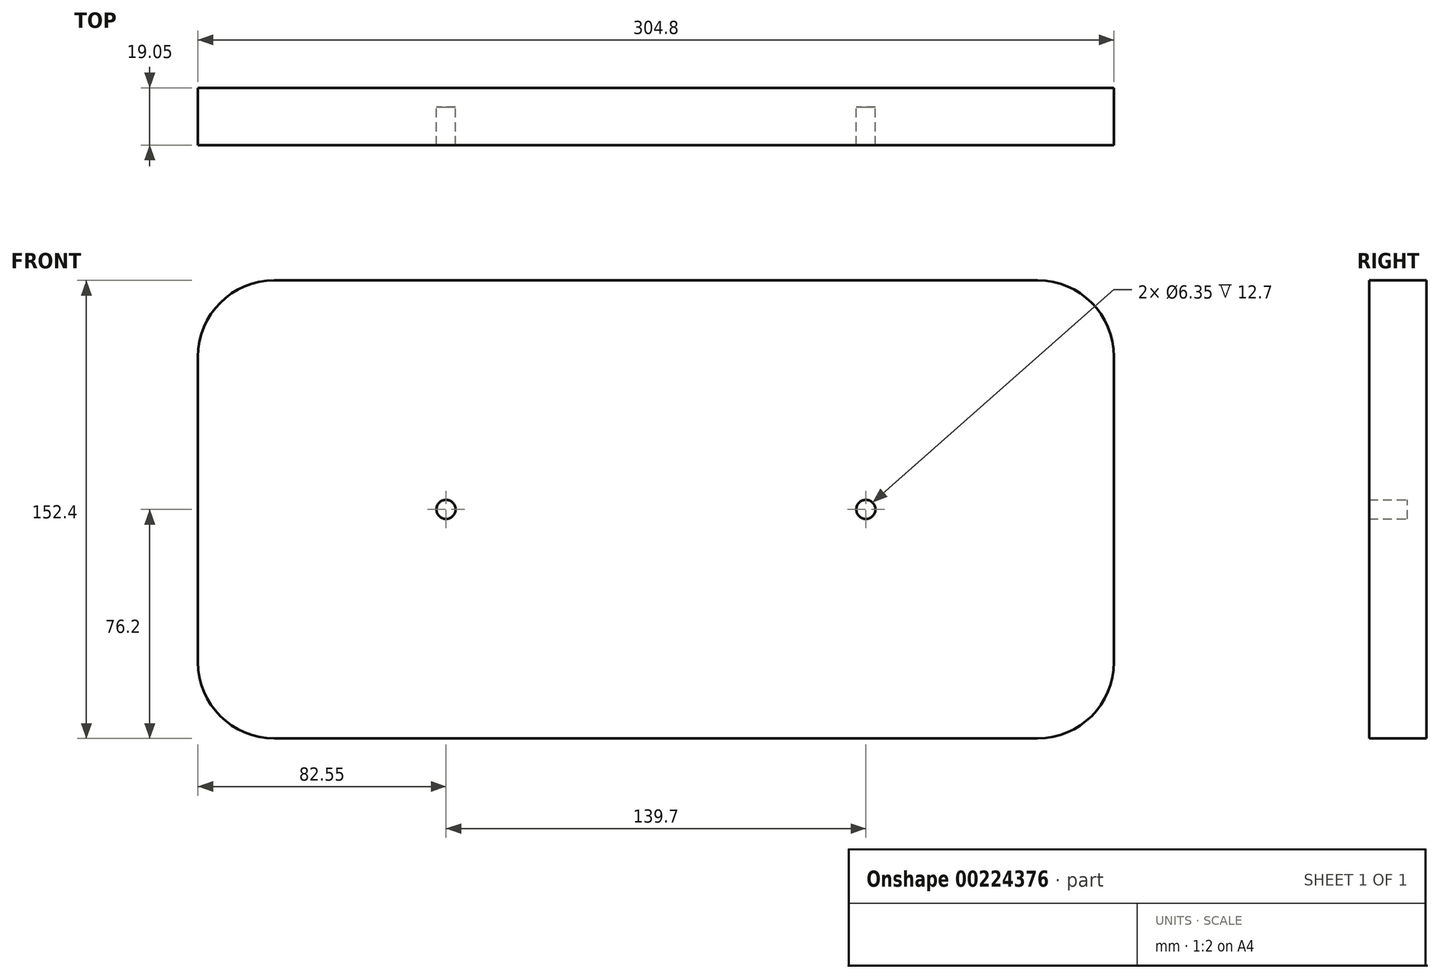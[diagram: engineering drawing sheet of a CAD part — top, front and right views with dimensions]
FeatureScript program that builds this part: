
annotation { "Feature Type Name" : "Feature", "Feature Type Description" : "" }
export const myFeature = defineFeature(function(context is Context, id is Id, definition is map)
    precondition{}
    {
        {
            var Q0;
            Q0=qCreatedBy(makeId("Front.planeOp"),FACE);
            var sketch = newSketch(context, id + "F0", { "sketchPlane" : qUnion([Q0])});
            skLineSegment(sketch, "E0.bottom", {"start": v(25.4, 0) * mm, "end": v(279.4, 0) * mm});
            skLineSegment(sketch, "E0.top", {"start": v(25.4, 152.4) * mm, "end": v(279.4, 152.4) * mm});
            skLineSegment(sketch, "E0.left", {"start": v(0, 25.4) * mm, "end": v(0, 127) * mm});
            skLineSegment(sketch, "E0.right", {"start": v(304.8, 25.4) * mm, "end": v(304.8, 127) * mm});
            skPoint(sketch, "E1.visualSharp", {"position": v(0, 0) * mm});
            skArc(sketch, "E1.filletArc", {"start": v(0, 25.4) * mm, "mid": v(7.44, 7.44) * mm, "end": v(25.4, 0) * mm});
            skPoint(sketch, "E2.visualSharp", {"position": v(0, 152.4) * mm});
            skArc(sketch, "E2.filletArc", {"start": v(25.4, 152.4) * mm, "mid": v(7.44, 144.96) * mm, "end": v(0, 127) * mm});
            skPoint(sketch, "E3.visualSharp", {"position": v(304.8, 152.4) * mm});
            skArc(sketch, "E3.filletArc", {"start": v(304.8, 127) * mm, "mid": v(297.36, 144.96) * mm, "end": v(279.4, 152.4) * mm});
            skPoint(sketch, "E4.visualSharp", {"position": v(304.8, 0) * mm});
            skArc(sketch, "E4.filletArc", {"start": v(279.4, 0) * mm, "mid": v(297.36, 7.44) * mm, "end": v(304.8, 25.4) * mm});
            skLineSegment(sketch, "E5.bottom", {"start": v(31.75, 146.05) * mm, "end": v(273.05, 146.05) * mm});
            skLineSegment(sketch, "E5.top", {"start": v(31.75, 6.35) * mm, "end": v(273.05, 6.35) * mm});
            skLineSegment(sketch, "E5.left", {"start": v(6.35, 120.65) * mm, "end": v(6.35, 31.75) * mm});
            skLineSegment(sketch, "E5.right", {"start": v(298.45, 120.65) * mm, "end": v(298.45, 31.75) * mm});
            skPoint(sketch, "E6.visualSharp", {"position": v(6.35, 146.05) * mm});
            skArc(sketch, "E6.filletArc", {"start": v(31.75, 146.05) * mm, "mid": v(13.79, 138.61) * mm, "end": v(6.35, 120.65) * mm});
            skPoint(sketch, "E7.visualSharp", {"position": v(6.35, 6.35) * mm});
            skArc(sketch, "E7.filletArc", {"start": v(6.35, 31.75) * mm, "mid": v(13.79, 13.79) * mm, "end": v(31.75, 6.35) * mm});
            skPoint(sketch, "E8.visualSharp", {"position": v(298.45, 146.05) * mm});
            skArc(sketch, "E8.filletArc", {"start": v(298.45, 120.65) * mm, "mid": v(291.01, 138.61) * mm, "end": v(273.05, 146.05) * mm});
            skPoint(sketch, "E9.visualSharp", {"position": v(298.45, 6.35) * mm});
            skArc(sketch, "E9.filletArc", {"start": v(273.05, 6.35) * mm, "mid": v(291.01, 13.79) * mm, "end": v(298.45, 31.75) * mm});
            skLineSegment(sketch, "E10", {"start": v(0, 76.2) * mm, "end": v(304.8, 76.2) * mm});
            skSolve(sketch);
        }
        {
            var Q0;
            Q0 = qSketchRegion(id + "F0", true);
            extrude(context, id + "F1", {"entities" : qUnion([Q0]), "depth" : 19.05 * mm});
        }
        {
            var Q0;
            Q0=makeQuery(id+"F0.imprint","IMPRINT",FACE,{"disambiguationData":[TD([[makeQuery(id+"F0.imprint","IMPRINT",EDGE,{"derivedFrom":sQuery(id+"F0.wireOp",EDGE,"E5.bottom")}),-1.0]])]});
            var Q1;
            Q1=makeQuery(id+"F0.imprint","IMPRINT",FACE,{"disambiguationData":[TD([[makeQuery(id+"F0.imprint","IMPRINT",EDGE,{"derivedFrom":sQuery(id+"F0.wireOp",EDGE,"E5.top")}),1.0]])]});
            extrude(context, id + "F2", {"entities" : qUnion([Q0, Q1]), "operationType" : NewBodyOperationType.ADD, "depth" : 6.35 * mm});
        }
        {
            var Q0;
            Q0=makeQuery(id+"F2.opExtrude","CAP_FACE",FACE,{"disambiguationData":[OSD([sQuery(id+"F0.wireOp",EDGE,"E5.bottom"),sQuery(id+"F0.wireOp",EDGE,"E5.top"),sQuery(id+"F0.wireOp",EDGE,"E5.left"),sQuery(id+"F0.wireOp",EDGE,"E5.right"),sQuery(id+"F0.wireOp",EDGE,"E6.filletArc"),sQuery(id+"F0.wireOp",EDGE,"E7.filletArc"),sQuery(id+"F0.wireOp",EDGE,"E8.filletArc"),sQuery(id+"F0.wireOp",EDGE,"E9.filletArc")])],"isStart":false});
            var sketch = newSketch(context, id + "F3", { "sketchPlane" : qUnion([Q0])});
            skLineSegment(sketch, "E11", {"start": v(6.35, 76.2) * mm, "end": v(298.45, 76.2) * mm});
            skCircle(sketch, "E12", {"center": v(82.55, 76.2) * mm, "radius": 3.18 * mm});
            skCircle(sketch, "E13", {"center": v(158.75, 76.2) * mm, "radius": 3.18 * mm});
            skCircle(sketch, "E14", {"center": v(222.25, 76.2) * mm, "radius": 3.18 * mm});
            skSolve(sketch);
        }
        {
            var Q0;
            {var subQ0=sQuery(id+"F3.wireOp",EDGE,"E12");var subQ1=sQuery(id+"F3.wireOp",EDGE,"E11");var subQ2=makeQuery(id+"F3.imprint","INTERSECT",VERTEX,{"disambiguationData":[OD(0.0)],"derivedFrom":[subQ1,subQ0]});Q0=makeQuery(id+"F3.imprint","IMPRINT",FACE,{"disambiguationData":[TD([[makeQuery(id+"F3.imprint","IMPRINT",EDGE,{"disambiguationData":[TD([[subQ2,-1.0]])],"derivedFrom":subQ1}),1.0]])]});}
            var Q1;
            {var subQ0=sQuery(id+"F3.wireOp",EDGE,"E12");var subQ1=sQuery(id+"F3.wireOp",EDGE,"E11");var subQ2=makeQuery(id+"F3.imprint","INTERSECT",VERTEX,{"disambiguationData":[OD(0.0)],"derivedFrom":[subQ1,subQ0]});Q1=makeQuery(id+"F3.imprint","IMPRINT",FACE,{"disambiguationData":[TD([[makeQuery(id+"F3.imprint","IMPRINT",EDGE,{"disambiguationData":[TD([[subQ2,-1.0]])],"derivedFrom":subQ1}),-1.0]])]});}
            var Q2;
            {var subQ0=sQuery(id+"F3.wireOp",EDGE,"E13");var subQ1=sQuery(id+"F3.wireOp",EDGE,"E11");var subQ2=makeQuery(id+"F3.imprint","INTERSECT",VERTEX,{"disambiguationData":[OD(0.0)],"derivedFrom":[subQ1,subQ0]});Q2=makeQuery(id+"F3.imprint","IMPRINT",FACE,{"disambiguationData":[TD([[makeQuery(id+"F3.imprint","IMPRINT",EDGE,{"disambiguationData":[TD([[subQ2,-1.0]])],"derivedFrom":subQ1}),-1.0]])]});}
            var Q3;
            {var subQ0=sQuery(id+"F3.wireOp",EDGE,"E13");var subQ1=sQuery(id+"F3.wireOp",EDGE,"E11");var subQ2=makeQuery(id+"F3.imprint","INTERSECT",VERTEX,{"disambiguationData":[OD(0.0)],"derivedFrom":[subQ1,subQ0]});Q3=makeQuery(id+"F3.imprint","IMPRINT",FACE,{"disambiguationData":[TD([[makeQuery(id+"F3.imprint","IMPRINT",EDGE,{"disambiguationData":[TD([[subQ2,-1.0]])],"derivedFrom":subQ1}),1.0]])]});}
            var Q4;
            {var subQ0=sQuery(id+"F3.wireOp",EDGE,"E14");var subQ1=sQuery(id+"F3.wireOp",EDGE,"E11");var subQ2=makeQuery(id+"F3.imprint","INTERSECT",VERTEX,{"disambiguationData":[OD(0.0)],"derivedFrom":[subQ1,subQ0]});Q4=makeQuery(id+"F3.imprint","IMPRINT",FACE,{"disambiguationData":[TD([[makeQuery(id+"F3.imprint","IMPRINT",EDGE,{"disambiguationData":[TD([[subQ2,-1.0]])],"derivedFrom":subQ1}),-1.0]])]});}
            var Q5;
            {var subQ0=sQuery(id+"F3.wireOp",EDGE,"E14");var subQ1=sQuery(id+"F3.wireOp",EDGE,"E11");var subQ2=makeQuery(id+"F3.imprint","INTERSECT",VERTEX,{"disambiguationData":[OD(0.0)],"derivedFrom":[subQ1,subQ0]});Q5=makeQuery(id+"F3.imprint","IMPRINT",FACE,{"disambiguationData":[TD([[makeQuery(id+"F3.imprint","IMPRINT",EDGE,{"disambiguationData":[TD([[subQ2,-1.0]])],"derivedFrom":subQ1}),1.0]])]});}
            extrude(context, id + "F4", {"entities" : qUnion([Q0, Q1, Q2, Q3, Q4, Q5]), "operationType" : NewBodyOperationType.ADD, "depth" : 12.7 * mm});
        }
    });
